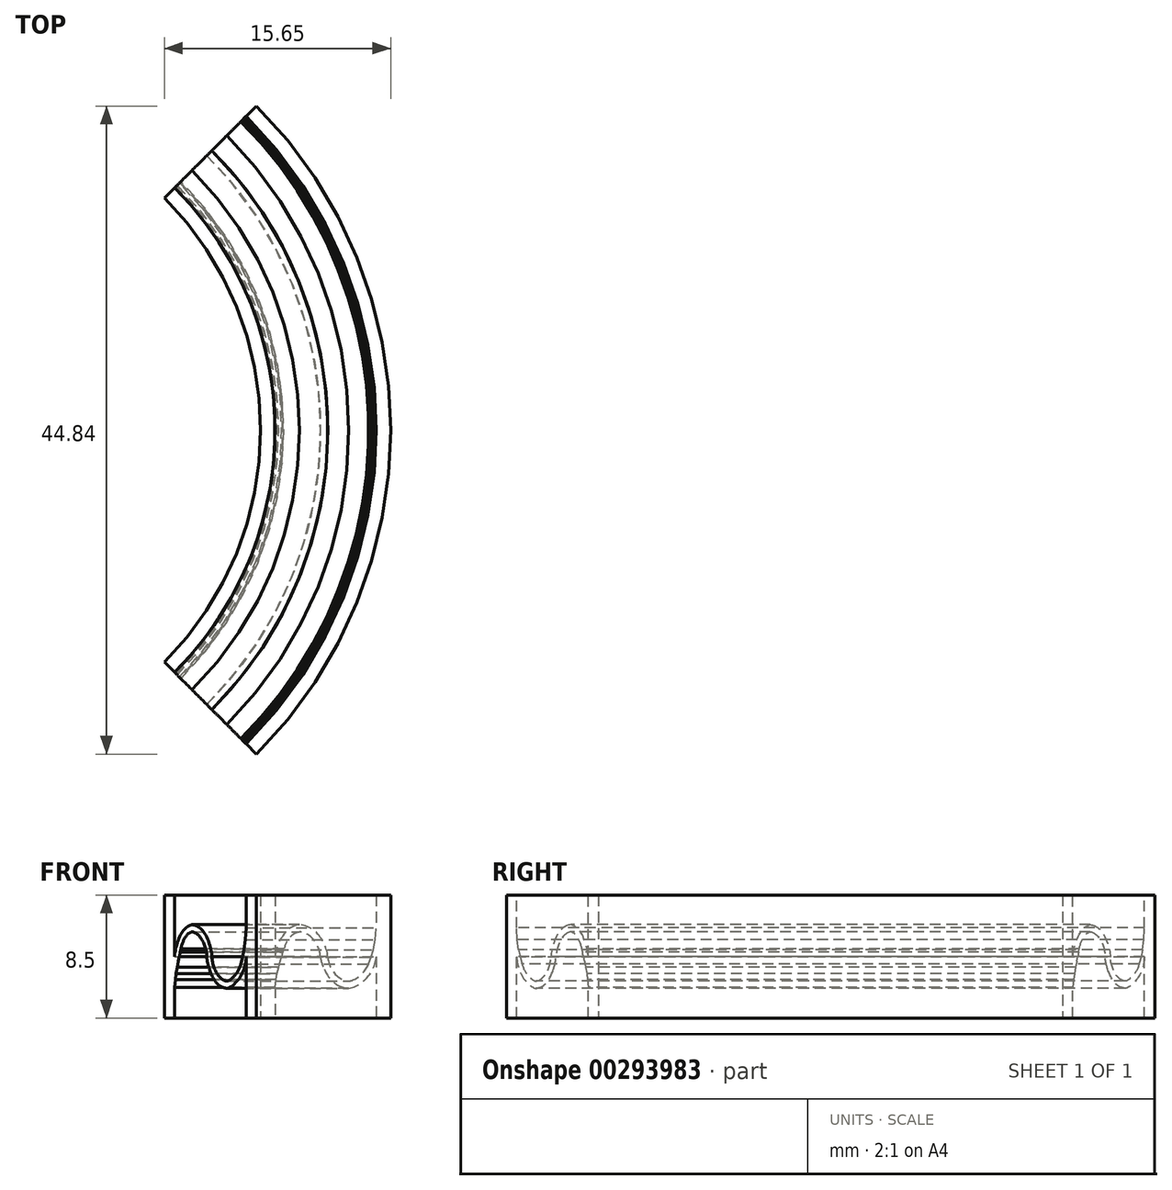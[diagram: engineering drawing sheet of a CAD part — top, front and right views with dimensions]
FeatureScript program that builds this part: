
annotation { "Feature Type Name" : "Feature", "Feature Type Description" : "" }
export const myFeature = defineFeature(function(context is Context, id is Id, definition is map)
    precondition{}
    {
        {
            var Q0;
            Q0=qCreatedBy(makeId("Front.planeOp"),FACE);
            var sketch = newSketch(context, id + "F0", { "sketchPlane" : qUnion([Q0])});
            skLineSegment(sketch, "E0", {"start": v(8, 0) * mm, "end": v(9, 0) * mm});
            skLineSegment(sketch, "E1", {"start": v(9, 8.5) * mm, "end": v(0, 8.5) * mm, "construction": true});
            skLineSegment(sketch, "E2", {"start": v(0, 8.5) * mm, "end": v(0, 0) * mm});
            skLineSegment(sketch, "E3", {"start": v(0, 0) * mm, "end": v(1, 0) * mm});
            skLineSegment(sketch, "E4", {"start": v(1, 0) * mm, "end": v(1, 8.5) * mm});
            skLineSegment(sketch, "E5", {"start": v(0, 0) * mm, "end": v(-0.5, 0) * mm});
            skLineSegment(sketch, "E6", {"start": v(1, 8.5) * mm, "end": v(1, 0) * mm});
            skLineSegment(sketch, "E7", {"start": v(1, 4.25) * mm, "end": v(6.1, 4.23) * mm, "construction": true});
            skLineSegment(sketch, "E8", {"start": v(1, 4.25) * mm, "end": v(2.7, 4.25) * mm, "construction": true});
            skLineSegment(sketch, "E9", {"start": v(0.94, 4.25) * mm, "end": v(2.64, 4.24) * mm, "construction": true});
            skLineSegment(sketch, "E10", {"start": v(2.7, 4.25) * mm, "end": v(2.7, 6.45) * mm, "construction": true});
            skLineSegment(sketch, "E11", {"start": v(0.94, 4.25) * mm, "end": v(0.94, 2.05) * mm, "construction": true});
            skFitSpline(sketch, "E12", {"points": [v(1, 4.25) * mm, v(1.6, 5.78) * mm, v(2.7, 6.45) * mm], "startDerivative": vector(0, 1.77) * mm, "endDerivative": vector(2.28, 0.15) * mm});
            skLineSegment(sketch, "E13", {"start": v(1, 4.25) * mm, "end": v(1.5, 4.25) * mm});
            skLineSegment(sketch, "E14", {"start": v(2.7, 6.45) * mm, "end": v(2.7, 5.95) * mm});
            skFitSpline(sketch, "E15", {"points": [v(1.5, 4.25) * mm, v(1.86, 5.34) * mm, v(2.7, 5.95) * mm], "startDerivative": vector(0.07, 1.51) * mm, "endDerivative": vector(2.13, 0.19) * mm});
            skFitSpline(sketch, "E16", {"points": [v(2.7, 5.95) * mm, v(3.73, 5.35) * mm, v(4.15, 4.25) * mm], "startDerivative": vector(2.26, -0.06) * mm, "endDerivative": vector(0.1, -2.09) * mm});
            skFitSpline(sketch, "E17", {"points": [v(2.7, 6.45) * mm, v(3.9, 5.89) * mm, v(4.65, 4.25) * mm], "startDerivative": vector(2.58, -0.22) * mm, "endDerivative": vector(-0.05, -2.13) * mm});
            skFitSpline(sketch, "E18.MirrorCS", {"points": [v(6.1, 2.55) * mm, v(5.07, 3.15) * mm, v(4.65, 4.25) * mm], "startDerivative": vector(-2.26, 0.06) * mm, "endDerivative": vector(-0.1, 2.09) * mm});
            skFitSpline(sketch, "E19.MirrorCS", {"points": [v(6.1, 2.05) * mm, v(4.9, 2.61) * mm, v(4.15, 4.25) * mm], "startDerivative": vector(-2.58, 0.22) * mm, "endDerivative": vector(0.05, 2.13) * mm});
            skFitSpline(sketch, "E20.MirrorCS", {"points": [v(7.59, 4.23) * mm, v(7.27, 3.34) * mm, v(6.1, 2.55) * mm], "startDerivative": vector(-0.07, -1.51) * mm, "endDerivative": vector(-2.13, -0.19) * mm});
            skFitSpline(sketch, "E21.MirrorCS", {"points": [v(8, 4.26) * mm, v(7.55, 3) * mm, v(6.1, 2.05) * mm], "startDerivative": vector(0, -1.77) * mm, "endDerivative": vector(-2.28, -0.15) * mm});
            skLineSegment(sketch, "E22", {"start": v(1.37, 3.94) * mm, "end": v(1.26, 3.52) * mm});
            skLineSegment(sketch, "E23", {"start": v(1.26, 3.52) * mm, "end": v(1.14, 3.07) * mm});
            skLineSegment(sketch, "E24", {"start": v(1.14, 3.07) * mm, "end": v(1.08, 2.67) * mm});
            skLineSegment(sketch, "E25", {"start": v(1.08, 2.67) * mm, "end": v(1, 2.12) * mm});
            skLineSegment(sketch, "E26", {"start": v(1.37, 3.94) * mm, "end": v(1.61, 4.78) * mm});
            skLineSegment(sketch, "E27", {"start": v(4.4, 4.25) * mm, "end": v(4.4, 2.68) * mm});
            skLineSegment(sketch, "E28", {"start": v(7.8, 4.71) * mm, "end": v(7.93, 5.43) * mm});
            skLineSegment(sketch, "E29", {"start": v(7.93, 5.43) * mm, "end": v(8, 6.23) * mm});
            skLineSegment(sketch, "E30", {"start": v(7.8, 4.71) * mm, "end": v(7.66, 4.23) * mm});
            skLineSegment(sketch, "E31", {"start": v(7.66, 4.23) * mm, "end": v(7.48, 3.73) * mm});
            skLineSegment(sketch, "E32", {"start": v(1, 8.5) * mm, "end": v(0, 8.5) * mm});
            skLineSegment(sketch, "E33", {"start": v(8, 0) * mm, "end": v(8, 8.5) * mm});
            skLineSegment(sketch, "E34", {"start": v(9, 0) * mm, "end": v(9, 8.5) * mm});
            skLineSegment(sketch, "E35", {"start": v(8, 8.5) * mm, "end": v(9, 8.5) * mm});
            skLineSegment(sketch, "E36", {"start": v(0, 8.5) * mm, "end": v(1, 8.5) * mm});
            skLineSegment(sketch, "E37", {"start": v(0, 8.5) * mm, "end": v(-0.5, 8.5) * mm});
            skLineSegment(sketch, "E38", {"start": v(0, 0) * mm, "end": v(-22.7, 0) * mm});
            skLineSegment(sketch, "E39", {"start": v(-22.7, 0) * mm, "end": v(-22.7, 5.52) * mm});
            skSolve(sketch);
        }
        {
            var Q0;
            {var subQ4=sQuery(id+"F0.wireOp",EDGE,"E0");Q0=makeQuery(id+"F0.imprint","IMPRINT",FACE,{"disambiguationData":[TD([[makeQuery(id+"F0.imprint","IMPRINT",EDGE,{"derivedFrom":subQ4}),1.0]])]});}
            var Q1;
            Q1=makeQuery(id+"F0.imprint","IMPRINT",FACE,{"disambiguationData":[TD([[makeQuery(id+"F0.imprint","IMPRINT",EDGE,{"derivedFrom":sQuery(id+"F0.wireOp",EDGE,"E2")}),1.0]])]});
            var Q2;
            {var subQ2=sQuery(id+"F0.wireOp",EDGE,"E12");Q2=makeQuery(id+"F0.imprint","IMPRINT",FACE,{"disambiguationData":[TD([[makeQuery(id+"F0.imprint","IMPRINT",EDGE,{"derivedFrom":subQ2}),-1.0]])]});}
            var Q3;
            {var subQ13=sQuery(id+"F0.wireOp",EDGE,"E14");Q3=makeQuery(id+"F0.imprint","IMPRINT",FACE,{"disambiguationData":[TD([[makeQuery(id+"F0.imprint","IMPRINT",EDGE,{"derivedFrom":subQ13}),1.0]])]});}
            var Q4;
            {var subQ0=sQuery(id+"F0.wireOp",EDGE,"E26");var subQ1=sQuery(id+"F0.wireOp",EDGE,"E15");var subQ2=makeQuery(id+"F0.imprint","INTERSECT",VERTEX,{"disambiguationData":[OD(0.0)],"derivedFrom":[subQ1,subQ0]});Q4=makeQuery(id+"F0.imprint","IMPRINT",FACE,{"disambiguationData":[TD([[makeQuery(id+"F0.imprint","IMPRINT",EDGE,{"disambiguationData":[TD([[subQ2,1.0]])],"derivedFrom":subQ1}),-1.0]])]});}
            var Q5;
            {var subQ5=sQuery(id+"F0.wireOp",EDGE,"E22");Q5=makeQuery(id+"F0.imprint","IMPRINT",FACE,{"disambiguationData":[TD([[makeQuery(id+"F0.imprint","IMPRINT",EDGE,{"derivedFrom":subQ5}),-1.0]])]});}
            var Q6;
            {var subQ0=sQuery(id+"F0.wireOp",EDGE,"E15");var subQ1=sQuery(id+"F0.wireOp",EDGE,"E13");var subQ2=makeQuery(id+"F0.imprint","INTERSECT",VERTEX,{"derivedFrom":[subQ1,subQ0]});Q6=makeQuery(id+"F0.imprint","IMPRINT",FACE,{"disambiguationData":[TD([[makeQuery(id+"F0.imprint","IMPRINT",EDGE,{"disambiguationData":[TD([[subQ2,1.0]])],"derivedFrom":subQ1}),1.0]])]});}
            var Q7;
            {var subQ0=sQuery(id+"F0.wireOp",EDGE,"E31");var subQ1=sQuery(id+"F0.wireOp",EDGE,"E20.MirrorCS");var subQ2=makeQuery(id+"F0.imprint","INTERSECT",VERTEX,{"disambiguationData":[OD(0.0)],"derivedFrom":[subQ1,subQ0]});Q7=makeQuery(id+"F0.imprint","IMPRINT",FACE,{"disambiguationData":[TD([[makeQuery(id+"F0.imprint","IMPRINT",EDGE,{"disambiguationData":[TD([[subQ2,-1.0]])],"derivedFrom":subQ1}),-1.0]])]});}
            var Q8;
            Q8=sQuery(id+"F0.wireOp",EDGE,"E6");
            var Q9;
            Q9=sQuery(id+"F0.wireOp",EDGE,"E2");
            var Q10;
            Q10=sQuery(id+"F0.wireOp",EDGE,"E33");
            var Q11;
            Q11=sQuery(id+"F0.wireOp",EDGE,"E34");
            var Q12;
            Q12=sQuery(id+"F0.wireOp",EDGE,"E29");
            var Q13;
            Q13=sQuery(id+"F0.wireOp",EDGE,"E27");
            var Q14;
            Q14=sQuery(id+"F0.wireOp",EDGE,"E19.MirrorCS");
            var Q15;
            Q15=sQuery(id+"F0.wireOp",EDGE,"E4");
            var Q16;
            Q16=sQuery(id+"F0.wireOp",EDGE,"E16");
            var Q17;
            Q17=sQuery(id+"F0.wireOp",EDGE,"E17");
            var Q18;
            Q18=sQuery(id+"F0.wireOp",EDGE,"E12");
            var Q19;
            Q19=sQuery(id+"F0.wireOp",EDGE,"E21.MirrorCS");
            var Q20;
            Q20=sQuery(id+"F0.wireOp",EDGE,"E18.MirrorCS");
            var Q21;
            Q21=sQuery(id+"F0.wireOp",EDGE,"E15");
            var Q22;
            Q22=sQuery(id+"F0.wireOp",EDGE,"E0");
            var Q23;
            Q23=sQuery(id+"F0.wireOp",EDGE,"E20.MirrorCS");
            var Q24;
            Q24=sQuery(id+"F0.wireOp",EDGE,"E28");
            var Q25;
            Q25=sQuery(id+"F0.wireOp",EDGE,"E24");
            var Q26;
            Q26=sQuery(id+"F0.wireOp",EDGE,"E25");
            var Q27;
            Q27=sQuery(id+"F0.wireOp",EDGE,"E23");
            var Q28;
            Q28=sQuery(id+"F0.wireOp",EDGE,"E26");
            var Q29;
            Q29=sQuery(id+"F0.wireOp",EDGE,"E35");
            var Q30;
            Q30=sQuery(id+"F0.wireOp",EDGE,"E3");
            var Q31;
            Q31=sQuery(id+"F0.wireOp",EDGE,"E30");
            var Q32;
            Q32=sQuery(id+"F0.wireOp",EDGE,"E31");
            var Q33;
            Q33=sQuery(id+"F0.wireOp",EDGE,"E35");
            var Q34;
            Q34=sQuery(id+"F0.wireOp",EDGE,"E5");
            var Q35;
            Q35=sQuery(id+"F0.wireOp",EDGE,"E13");
            var Q36;
            Q36=sQuery(id+"F0.wireOp",EDGE,"E36");
            var Q37;
            Q37=sQuery(id+"F0.wireOp",EDGE,"E22");
            var Q38;
            Q38=sQuery(id+"F0.wireOp",EDGE,"E32");
            var Q39;
            Q39=sQuery(id+"F0.wireOp",EDGE,"E37");
            var Q40;
            Q40=sQuery(id+"F0.wireOp",EDGE,"E14");
            var Q41;
            Q41=sQuery(id+"F0.wireOp",EDGE,"E39");
            revolve(context, id + "F1", {"entities" : qUnion([Q0, Q1, Q2, Q3, Q4, Q5, Q6, Q7]), "surfaceEntities" : qUnion([Q8, Q9, Q10, Q11, Q12, Q13, Q14, Q15, Q16, Q17, Q18, Q19, Q20, Q21, Q22, Q23, Q24, Q25, Q26, Q27, Q28, Q29, Q30, Q31, Q32, Q33, Q34, Q35, Q36, Q37, Q38, Q39, Q40]), "axis" : qUnion([Q41]), "revolveType" : RevolveType.SYMMETRIC, "angle" : 90 * degree});
        }
    });
